# Revit family: X280 series non-automatic
name_source: partatom
category: Mechanical Equipment
revit_build: Autodesk Revit 2013 (Build: 20120221_2030(x64)
units: mm (PartAtom-declared; Revit-internal decimal feet)

## types (13) — shared parameters
Assembly Code = D2010900
Cooling = Oil Filled
Cord Length = 240"
Cord Type = UL listed, 5-wire (1 Ph)
Default Elevation = 0"
Description = Commercial Effluent Pumps
Discharge Diameter = 2" or 3" NPT Flange
Discharge Height = 6 5/16"
Discharge Radius = 1"
Hertz = 60
Impeller Type = Non-clogging vortex
Installation Type = Floor Mounted
Insulation = Class B
Length = 13 9/16"
Manufacturer = Zoeller
Masterformat Number = 33 36 16
Masterformat Title = Utility Septic Tank Effluent Pumps
Material = Cast Iron-Zoeller-Powder Coated Epoxy
Max. Operating Temp. = 104° F
Mechanical Seals = Carbon and ceramic with stainless steel parts
Model = X282
Motor Thermal Shutoff = Thermal Overload (1 Ph)
Motor Type = Submersible
Omniclass Table 23 Code = 23.60.30.21
Omniclass Table 23 Title = Pumps
Operation = Non-Automatic
Overall Height = 23 17/32"
Price = Prices may vary. Please consult Manufacturer Representative for most up-to-date price list.
Product Page URL = http://www.zoellerpumps.com
RPM = 1750
Solid Handling = 2" Spherical Solids
Square Ring & Gasket = Neoprene
Type = Permanent Split Capacitor
URL = http://www.zoellerengprod.com
Warranty Information = 36 Months (Limited)
Waste Connection = Yes
Weight = 124-127 lbs.
Width = 10"

## per-type parameters (varying)
| type | Amps | Apparent Load | Flow @ 5' | Impeller Diameter | Maximum Head | Motor | Phase | Voltage |
| X282-115V 1Ph | 10 A | 1185 VA | 127 GPM | 6 1/4" | 312" | 1/2 HP | 1 Ph | 115 V |
| X284-200V 1Ph | 9 A | 1860 VA | 179 GPM | 6 1/2" | 420" | 1 HP | 1 Ph | 200 V |
| X282-200V 1Ph | 6 A | 1220 VA | 127 GPM | 6 1/4" | 312" | 1/2 HP | 1 Ph | 200 V |
| X282-200V 3Ph | 4 A | 720 VA | 127 GPM | 6 1/4" | 312" | 1/2 HP | 3 Ph | 200 V |
| X282-230V 3Ph | 3 A | 690 VA | 127 GPM | 6 1/4" | 312" | 1/2 HP | 3 Ph | 230 V |
| X282-230V 1Ph | 5 A | 1150 VA | 127 GPM | 6 1/4" | 312" | 1/2 HP | 1 Ph | 230 V |
| X282-460V 3Ph | 2 A | 782 VA | 127 GPM | 6 1/4" | 312" | 1/2 HP | 3 Ph | 460 V |
| X282-575V 3Ph | 1 A | 805 VA | 127 GPM | 6 1/4" | 312" | 1/2 HP | 3 Ph | 575 V |
| X284-200V 3Ph | 6 A | 1100 VA | 179 GPM | 6 1/2" | 420" | 1 HP | 3 Ph | 200 V |
| X284-230V 1Ph | 9 A | 2047 VA | 179 GPM | 6 1/2" | 420" | 1 HP | 1 Ph | 230 V |
| X284-230V 3Ph | 5 A | 1150 VA | 179 GPM | 6 1/2" | 420" | 1 HP | 3 Ph | 230 V |
| X284-460V 3Ph | 3 A | 1196 VA | 179 GPM | 6 1/2" | 420" | 1 HP | 3 Ph | 460 V |
| X284-575V 3Ph | 2 A | 1265 VA | 179 GPM | 6 1/2" | 420" | 1 HP | 3 Ph | 575 V |

## geometry (parser evidence)
native form markers: Blend x4, Sweep x2
no freeform markers — native parametric forms only
